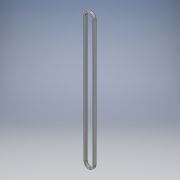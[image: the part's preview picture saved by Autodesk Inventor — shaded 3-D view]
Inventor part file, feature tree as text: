
AUTODESK INVENTOR PART (.ipt)
format: ipt  version: 2016 (Build 200138000, 138)  size: 116,736 bytes
history: native  units: in
note: dims shown in document units (in); Inventor stores cm internally (conversion verified against a paired STEP export)
features: fillet x4, shell x2, extrude x1, sketch x1
ambient origin geometry x8: Origin, YZ Plane, XZ Plane, XY Plane, X Axis, Y Axis, Z Axis, Center Point
bodies: Solid1 (feature_tree)
feature tree (8):
  extrude  "Extrusion1"  Depth=0.25in TaperAngle=0.0deg
  fillet  "Fillet1"  Radius=0.5in
  fillet  "Fillet2"  Radius=0.5in
  fillet  "Fillet3"  Radius=0.5in
  fillet  "Fillet4"  Radius=0.5in
  shell  "Shell1"  Thickness=0.1in
  shell  "Shell2"  Thickness=0.1in
  sketch  "Sketch1"  dims[d0=14.0in d1=0.25in d2=0.0in d3=0.5in d4=0.5in d5=0.5in d6=0.5in d7=0.1in d8=0.1in]
